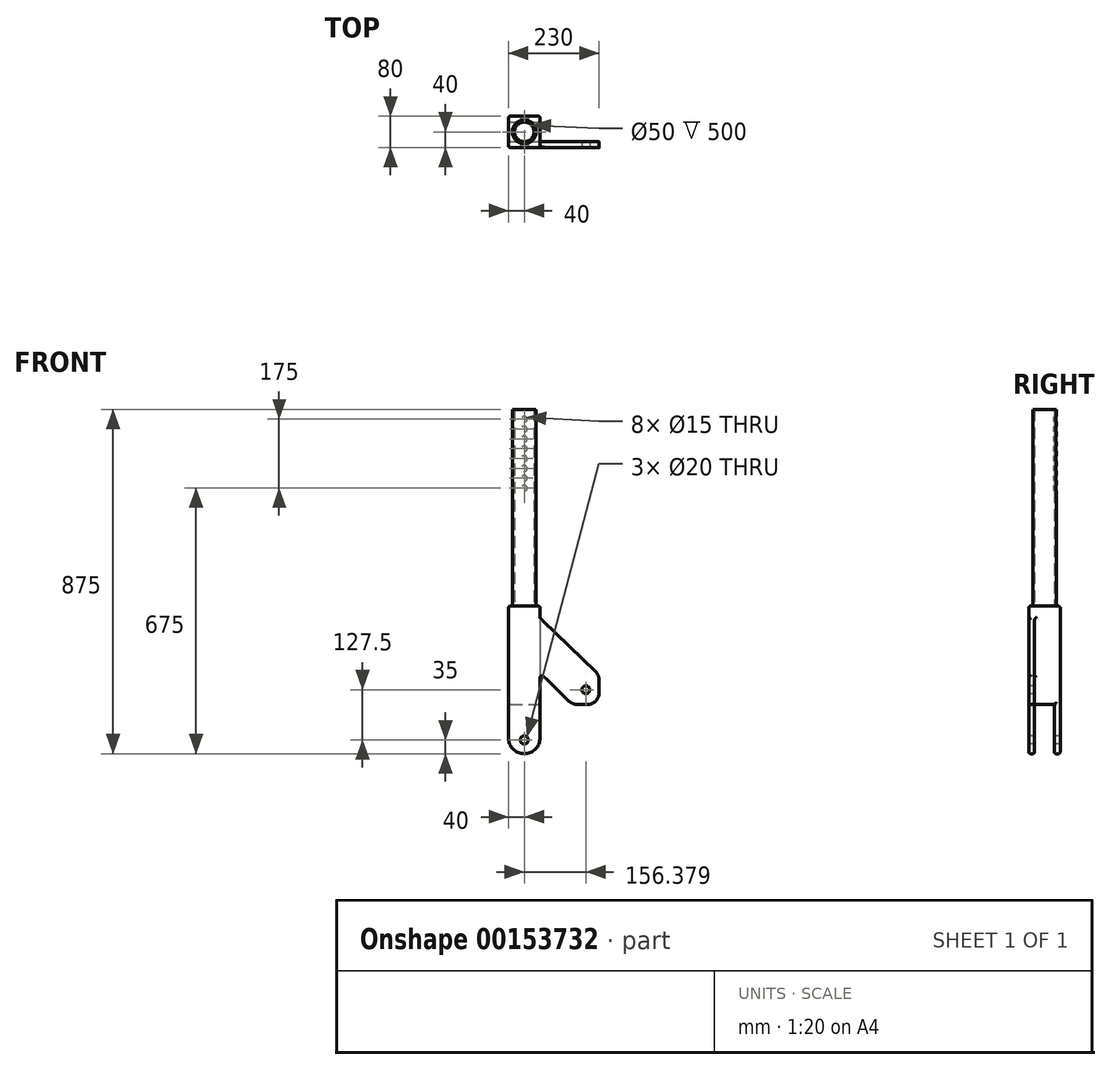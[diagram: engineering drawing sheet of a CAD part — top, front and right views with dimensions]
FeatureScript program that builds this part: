
annotation { "Feature Type Name" : "Feature", "Feature Type Description" : "" }
export const myFeature = defineFeature(function(context is Context, id is Id, definition is map)
    precondition{}
    {
        {
            var Q0;
            Q0=qCreatedBy(makeId("Top.planeOp"),FACE);
            var sketch = newSketch(context, id + "F0", { "sketchPlane" : qUnion([Q0])});
            skLineSegment(sketch, "E0.bottom", {"start": v(-40, -40) * mm, "end": v(40, -40) * mm});
            skLineSegment(sketch, "E0.top", {"start": v(-40, 40) * mm, "end": v(40, 40) * mm});
            skLineSegment(sketch, "E0.left", {"start": v(-40, -40) * mm, "end": v(-40, 40) * mm});
            skLineSegment(sketch, "E0.right", {"start": v(40, -40) * mm, "end": v(40, 40) * mm});
            skSolve(sketch);
        }
        {
            var Q0;
            Q0 = qSketchRegion(id + "F0", true);
            extrude(context, id + "F1", {"entities" : qUnion([Q0]), "depth" : 250 * mm});
        }
        {
            var Q0;
            Q0=makeQuery(id+"F1.opExtrude","CAP_FACE",FACE,{"disambiguationData":[OSD([sQuery(id+"F0.wireOp",EDGE,"E0.bottom"),sQuery(id+"F0.wireOp",EDGE,"E0.top"),sQuery(id+"F0.wireOp",EDGE,"E0.left"),sQuery(id+"F0.wireOp",EDGE,"E0.right")])],"isStart":false});
            var sketch = newSketch(context, id + "F2", { "sketchPlane" : qUnion([Q0])});
            skCircle(sketch, "E1", {"center": v(0, 0) * mm, "radius": 30 * mm});
            skCircle(sketch, "E2", {"center": v(0, 0) * mm, "radius": 25 * mm});
            skSolve(sketch);
        }
        {
            var Q0;
            Q0 = qSketchRegion(id + "F2", true);
            extrude(context, id + "F3", {"entities" : qUnion([Q0]), "operationType" : NewBodyOperationType.ADD, "depth" : 500 * mm});
        }
        {
            var Q0;
            Q0=qCreatedBy(makeId("Front.planeOp"),FACE);
            var sketch = newSketch(context, id + "F4", { "sketchPlane" : qUnion([Q0])});
            skLineSegment(sketch, "E3", {"start": v(0, 0) * mm, "end": v(0, 1100) * mm, "construction": true});
            skCircle(sketch, "E4", {"center": v(0, 725) * mm, "radius": 7.5 * mm});
            skCircle(sketch, "E5", {"center": v(0, 700) * mm, "radius": 7.5 * mm});
            skCircle(sketch, "E6", {"center": v(0, 675) * mm, "radius": 7.5 * mm});
            skCircle(sketch, "E7", {"center": v(0, 650) * mm, "radius": 7.5 * mm});
            skCircle(sketch, "E8", {"center": v(0, 625) * mm, "radius": 7.5 * mm});
            skCircle(sketch, "E9", {"center": v(0, 600) * mm, "radius": 7.5 * mm});
            skCircle(sketch, "E10", {"center": v(0, 575) * mm, "radius": 7.5 * mm});
            skCircle(sketch, "E11", {"center": v(0, 550) * mm, "radius": 7.5 * mm});
            skSolve(sketch);
        }
        {
            var Q0;
            Q0 = qSketchRegion(id + "F4", true);
            extrude(context, id + "F5", {"entities" : qUnion([Q0]), "operationType" : NewBodyOperationType.REMOVE, "endBound" : BoundingType.THROUGH_ALL, "oppositeDirection" : true, "depth" : 25 * mm});
        }
        {
            var Q0;
            Q0=makeQuery(id+"F1.opExtrude","SWEPT_FACE",FACE,{"disambiguationData":[OSD([sQuery(id+"F0.wireOp",EDGE,"E0.bottom")])]});
            var sketch = newSketch(context, id + "F6", { "sketchPlane" : qUnion([Q0])});
            skLineSegment(sketch, "E12", {"start": v(40, 80) * mm, "end": v(122.76, 0) * mm});
            skLineSegment(sketch, "E13", {"start": v(122.76, 0) * mm, "end": v(190, 0) * mm});
            skLineSegment(sketch, "E14", {"start": v(190, 0) * mm, "end": v(190, 75) * mm});
            skLineSegment(sketch, "E15", {"start": v(190, 75) * mm, "end": v(40, 220) * mm});
            skLineSegment(sketch, "E16", {"start": v(40, 220) * mm, "end": v(40, 80) * mm});
            skSolve(sketch);
        }
        {
            var Q0;
            Q0 = qSketchRegion(id + "F6", true);
            extrude(context, id + "F7", {"entities" : qUnion([Q0]), "operationType" : NewBodyOperationType.ADD, "oppositeDirection" : true, "depth" : 15 * mm});
        }
        {
            var Q0;
            Q0=makeQuery(id+"F1.opExtrude","CAP_FACE",FACE,{"disambiguationData":[OSD([sQuery(id+"F0.wireOp",EDGE,"E0.bottom"),sQuery(id+"F0.wireOp",EDGE,"E0.top"),sQuery(id+"F0.wireOp",EDGE,"E0.left"),sQuery(id+"F0.wireOp",EDGE,"E0.right")])],"isStart":true});
            var sketch = newSketch(context, id + "F8", { "sketchPlane" : qUnion([Q0])});
            skLineSegment(sketch, "E17.bottom", {"start": v(-40, 40) * mm, "end": v(40, 40) * mm});
            skLineSegment(sketch, "E17.top", {"start": v(-40, 25) * mm, "end": v(40, 25) * mm});
            skLineSegment(sketch, "E17.left", {"start": v(-40, 40) * mm, "end": v(-40, 25) * mm});
            skLineSegment(sketch, "E17.right", {"start": v(40, 40) * mm, "end": v(40, 25) * mm});
            skLineSegment(sketch, "E18.bottom", {"start": v(-40, -40) * mm, "end": v(40, -40) * mm});
            skLineSegment(sketch, "E18.top", {"start": v(-40, -25) * mm, "end": v(40, -25) * mm});
            skLineSegment(sketch, "E18.left", {"start": v(-40, -40) * mm, "end": v(-40, -25) * mm});
            skLineSegment(sketch, "E18.right", {"start": v(40, -40) * mm, "end": v(40, -25) * mm});
            skSolve(sketch);
        }
        {
            var Q0;
            Q0 = qSketchRegion(id + "F8", true);
            extrude(context, id + "F9", {"entities" : qUnion([Q0]), "operationType" : NewBodyOperationType.ADD, "depth" : 125 * mm});
        }
        {
            var Q0;
            Q0=makeQuery(id+"F9.boolean.opBoolean","MERGE",FACE,{"derivedFrom":[makeQuery(id+"F7.boolean.opBoolean","MERGE",FACE,{"derivedFrom":[makeQuery(id+"F1.opExtrude","SWEPT_FACE",FACE,{"disambiguationData":[OSD([sQuery(id+"F0.wireOp",EDGE,"E0.bottom")])]}),makeQuery(id+"F7.opExtrude","CAP_FACE",FACE,{"disambiguationData":[OSD([sQuery(id+"F6.wireOp",EDGE,"E12"),sQuery(id+"F6.wireOp",EDGE,"E13"),sQuery(id+"F6.wireOp",EDGE,"E14"),sQuery(id+"F6.wireOp",EDGE,"E15"),sQuery(id+"F6.wireOp",EDGE,"E16")])],"isStart":true})]}),makeQuery(id+"F9.opExtrude","SWEPT_FACE",FACE,{"disambiguationData":[OSD([sQuery(id+"F8.wireOp",EDGE,"E17.bottom")])]})]});
            var sketch = newSketch(context, id + "F10", { "sketchPlane" : qUnion([Q0])});
            skCircle(sketch, "E19", {"center": v(156.38, 37.5) * mm, "radius": 10 * mm});
            skCircle(sketch, "E20", {"center": v(0, -90) * mm, "radius": 10 * mm});
            skPoint(sketch, "E21", {"position": v(156.38, 0) * mm});
            skPoint(sketch, "E22", {"position": v(190, 37.5) * mm});
            skSolve(sketch);
        }
        {
            var Q0;
            Q0 = qSketchRegion(id + "F10", true);
            extrude(context, id + "F11", {"entities" : qUnion([Q0]), "operationType" : NewBodyOperationType.REMOVE, "endBound" : BoundingType.THROUGH_ALL, "oppositeDirection" : true, "depth" : 25 * mm});
        }
        {
            var Q0;
            Q0=makeQuery(id+"F7.opExtrude","SWEPT_EDGE",EDGE,{"disambiguationData":[OSD([sQuery(id+"F0.wireOp",EDGE,"E0.bottom"),sQuery(id+"F0.wireOp",EDGE,"E0.right"),sQuery(id+"F6.wireOp",EDGE,"E15"),sQuery(id+"F6.wireOp",EDGE,"E16")])]});
            var Q1;
            Q1=makeQuery(id+"F2KEcn6DbPgbOMS_1.1.F7.opExtrude","SWEPT_EDGE",EDGE,{"disambiguationData":[OSD([sQuery(id+"F0.wireOp",EDGE,"E0.bottom"),sQuery(id+"F0.wireOp",EDGE,"E0.right"),sQuery(id+"F6.wireOp",EDGE,"E15"),sQuery(id+"F6.wireOp",EDGE,"E16")])]});
            var Q2;
            Q2=makeQuery(id+"F7.opExtrude","SWEPT_EDGE",EDGE,{"disambiguationData":[OSD([sQuery(id+"F6.wireOp",EDGE,"E14"),sQuery(id+"F6.wireOp",EDGE,"E15")])]});
            var Q3;
            Q3=makeQuery(id+"F2KEcn6DbPgbOMS_1.1.F7.opExtrude","SWEPT_EDGE",EDGE,{"disambiguationData":[OSD([sQuery(id+"F6.wireOp",EDGE,"E14"),sQuery(id+"F6.wireOp",EDGE,"E15")])]});
            var Q4;
            Q4=makeQuery(id+"F7.opExtrude","SWEPT_EDGE",EDGE,{"disambiguationData":[OSD([sQuery(id+"F6.wireOp",EDGE,"E13"),sQuery(id+"F6.wireOp",EDGE,"E14")])]});
            var Q5;
            Q5=makeQuery(id+"F2KEcn6DbPgbOMS_1.1.F7.opExtrude","SWEPT_EDGE",EDGE,{"disambiguationData":[OSD([sQuery(id+"F6.wireOp",EDGE,"E13"),sQuery(id+"F6.wireOp",EDGE,"E14")])]});
            var Q6;
            Q6=makeQuery(id+"F2KEcn6DbPgbOMS_1.1.F7.opExtrude","SWEPT_EDGE",EDGE,{"disambiguationData":[OSD([sQuery(id+"F6.wireOp",EDGE,"E12"),sQuery(id+"F6.wireOp",EDGE,"E13")])]});
            var Q7;
            Q7=makeQuery(id+"F7.opExtrude","SWEPT_EDGE",EDGE,{"disambiguationData":[OSD([sQuery(id+"F6.wireOp",EDGE,"E12"),sQuery(id+"F6.wireOp",EDGE,"E13")])]});
            fillet(context, id + "F12", {"entities" : qUnion([Q0, Q1, Q2, Q3, Q4, Q5, Q6, Q7]), "radius" : 30 * mm, "tangentPropagation" : true, "allowEdgeOverflow" : false});
        }
        {
            var Q0;
            Q0=makeQuery(id+"F9.opExtrude","CAP_EDGE",EDGE,{"disambiguationData":[OSD([sQuery(id+"F8.wireOp",EDGE,"E17.left")])],"isStart":false});
            var Q1;
            Q1=makeQuery(id+"F9.opExtrude","CAP_EDGE",EDGE,{"disambiguationData":[OSD([sQuery(id+"F8.wireOp",EDGE,"E17.right")])],"isStart":false});
            var Q2;
            Q2=makeQuery(id+"F9.opExtrude","CAP_EDGE",EDGE,{"disambiguationData":[OSD([sQuery(id+"F8.wireOp",EDGE,"E18.left")])],"isStart":false});
            var Q3;
            Q3=makeQuery(id+"F9.opExtrude","CAP_EDGE",EDGE,{"disambiguationData":[OSD([sQuery(id+"F8.wireOp",EDGE,"E18.right")])],"isStart":false});
            fillet(context, id + "F13", {"entities" : qUnion([Q0, Q1, Q2, Q3]), "radius" : 40 * mm, "tangentPropagation" : true, "allowEdgeOverflow" : false});
        }
        {
            var Q0;
            Q0=makeQuery(id+"F1.opExtrude","CAP_EDGE",EDGE,{"disambiguationData":[OSD([sQuery(id+"F0.wireOp",EDGE,"E0.bottom")])],"isStart":false});
            var Q1;
            Q1=makeQuery(id+"F1.opExtrude","CAP_EDGE",EDGE,{"disambiguationData":[OSD([sQuery(id+"F0.wireOp",EDGE,"E0.right")])],"isStart":false});
            var Q2;
            {var subQ0=sQuery(id+"F0.wireOp",EDGE,"E0.right");var subQ1=sQuery(id+"F0.wireOp",EDGE,"E0.left");var subQ2=sQuery(id+"F0.wireOp",EDGE,"E0.top");var subQ3=sQuery(id+"F0.wireOp",EDGE,"E0.bottom");Q2=makeQuery(id+"F3.boolean.opBoolean","SPLIT",FACE,{"disambiguationData":[TD([makeQuery(id+"F1.opExtrude","SWEPT_FACE",FACE,{"disambiguationData":[OSD([subQ3])]})])],"derivedFrom":makeQuery(id+"F1.opExtrude","CAP_FACE",FACE,{"disambiguationData":[OSD([subQ3,subQ2,subQ1,subQ0])],"isStart":false})});}
            var Q3;
            Q3=makeQuery(id+"F9.boolean.opBoolean","MERGE",FACE,{"derivedFrom":[makeQuery(id+"F1.opExtrude","SWEPT_FACE",FACE,{"disambiguationData":[OSD([sQuery(id+"F0.wireOp",EDGE,"E0.right")])]}),makeQuery(id+"F9.opExtrude","SWEPT_FACE",FACE,{"disambiguationData":[OSD([sQuery(id+"F8.wireOp",EDGE,"E17.right")])]}),makeQuery(id+"F9.opExtrude","SWEPT_FACE",FACE,{"disambiguationData":[OSD([sQuery(id+"F8.wireOp",EDGE,"E18.right")])]})]});
            fillet(context, id + "F14", {"entities" : qUnion([Q0, Q1, Q2, Q3]), "radius" : 5 * mm, "tangentPropagation" : true, "allowEdgeOverflow" : false});
        }
    });
